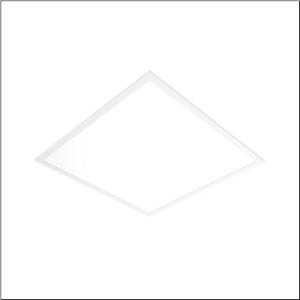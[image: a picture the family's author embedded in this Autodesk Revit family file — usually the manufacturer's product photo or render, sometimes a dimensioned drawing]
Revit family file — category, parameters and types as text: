
# Revit family: apollon_r__41_51mh11w72422_84d9
name_source: partatom
category: Lighting Fixtures
units: mm (PartAtom-declared; Revit-internal decimal feet)

## family parameters
Cut with Voids When Loaded = No
Host = Face
Light Source = No
Part Type = Normal
Room Calculation Point = No
Round Connector Dimension = Use Diameter
Shared = No

## types (1)
- Apollon® 41 (1 x LED, 3700 lm, 35 W, 4000K)
    Apparent Load = 35 VA
    CIE Flux Codes = 62 87 97 100 100
    Color Rendering = 80
    Color Temperature = 4000K
    Default Elevation = 1800 mm
    Description = Apollon® 41, office luminaire, primary optical cover: prismatic diffuser, of PS, light emission: direct distribution, primary light characteristic: symmetric, installation type: lay-in mounting, LED, rated luminous flux: 3.700lm, luminous efficacy: 105lm/W, light colour: 840, colour temperature: 4000K, control gear: ECG, with terminal, 3-pole, mains connection: 220..240V, AC, 50/60Hz, rated input power: 35W, housing, of aluminium section, traffic white (RAL 9016), module: M625, length: 620mm, width: 620mm, height: 32mm, housing upper side, of sheet steel, protection rating (complete): IP20, protection rating (lamp compartment, on room side): IP40, insulation class (complete): insulation class II (safety insulation), certification: CE, ENEC, permissible operating ambient temperature: -20..+40°C, packaging unit: 1 piece
    Height = 0 mm  [stored 0 ft]
    Lamp = 1 x LED
    Lamp Light Flux = 3700 lm
    Lamp Power = 35 W
    Lamp count = 1
    Length = 620 mm
    Luminous efficacy = 106 lm/W
    Manufacturer = Siteco
    ModVariant = No
    Model = 51MH11W72422
    Mounting Place = Ceiling
    Mounting Type = Recessed
    Number of Poles = 1
    OnlyDefault = Yes
    Power Factor = 1
    Product Name = Apollon® 41
    Product group = office luminaire | ceiling recessed
    ProductGroupID = 401
    Protection Class = Protection class II
    Protection Degree = IP 20
    RLX_Detail_Level = 1
    RLX_Emergency_Light_Flux = 0 lm
    RLX_Emergency_Type = 0
    RLX_Emergency_Type_DB = No
    RlxData = <blob elided: 14885 chars, md5=94faad15>
    Socket = socket
    Standby Power = 0 W
    System Light Flux = 3700 lm
    System Power = 35 W
    Type Comments = Product without accessories
    Type Image = l_1291024.jpg
    URL = http://relux.com
    VarID = ---
    Voltage = 0 V
    Weight = 0.00 kg
    Width = 620 mm

note: [stored X ft] marks values corroborated as IEEE doubles in the binary element streams (Revit-internal decimal feet)

## geometry (parser evidence)
native form markers: Sweep x10
no freeform markers — native parametric forms only
